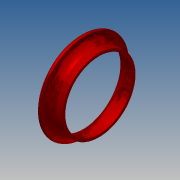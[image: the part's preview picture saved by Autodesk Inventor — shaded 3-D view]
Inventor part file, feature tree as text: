
AUTODESK INVENTOR PART (.ipt)
format: ipt  version: 2017.3 (Build 213257000, 257)  size: 181,248 bytes
history: native  units: in
note: dims shown in document units (in); Inventor stores cm internally (conversion verified against a paired STEP export)
features: other x3, extrude x2, sketch x1
ambient origin geometry x8: Origin, YZ Plane, XZ Plane, XY Plane, X Axis, Y Axis, Z Axis, Center Point
bodies: Solid1 (feature_tree)
feature tree (6):
  other  "A1-19027-500-02 HCWI nozzle horn.ipt"
  sketch  "Sketch2"  dims[d0=0.3937in d1=0.5in d2=0.5in d3=0.0in d4=0.0in d5=0.5in d6=2.125in d7=0.0in d8=0.0in]
  extrude  "Extrusion1"  Depth=0.3937in TaperAngle=0.0deg
  extrude  "Extrusion2"  Depth=0.3937in TaperAngle=0.0deg
  other  "Solid1::A1-19027-500-02 HCWI nozzle horn.ipt"
  other  "TaggingFeature1"
